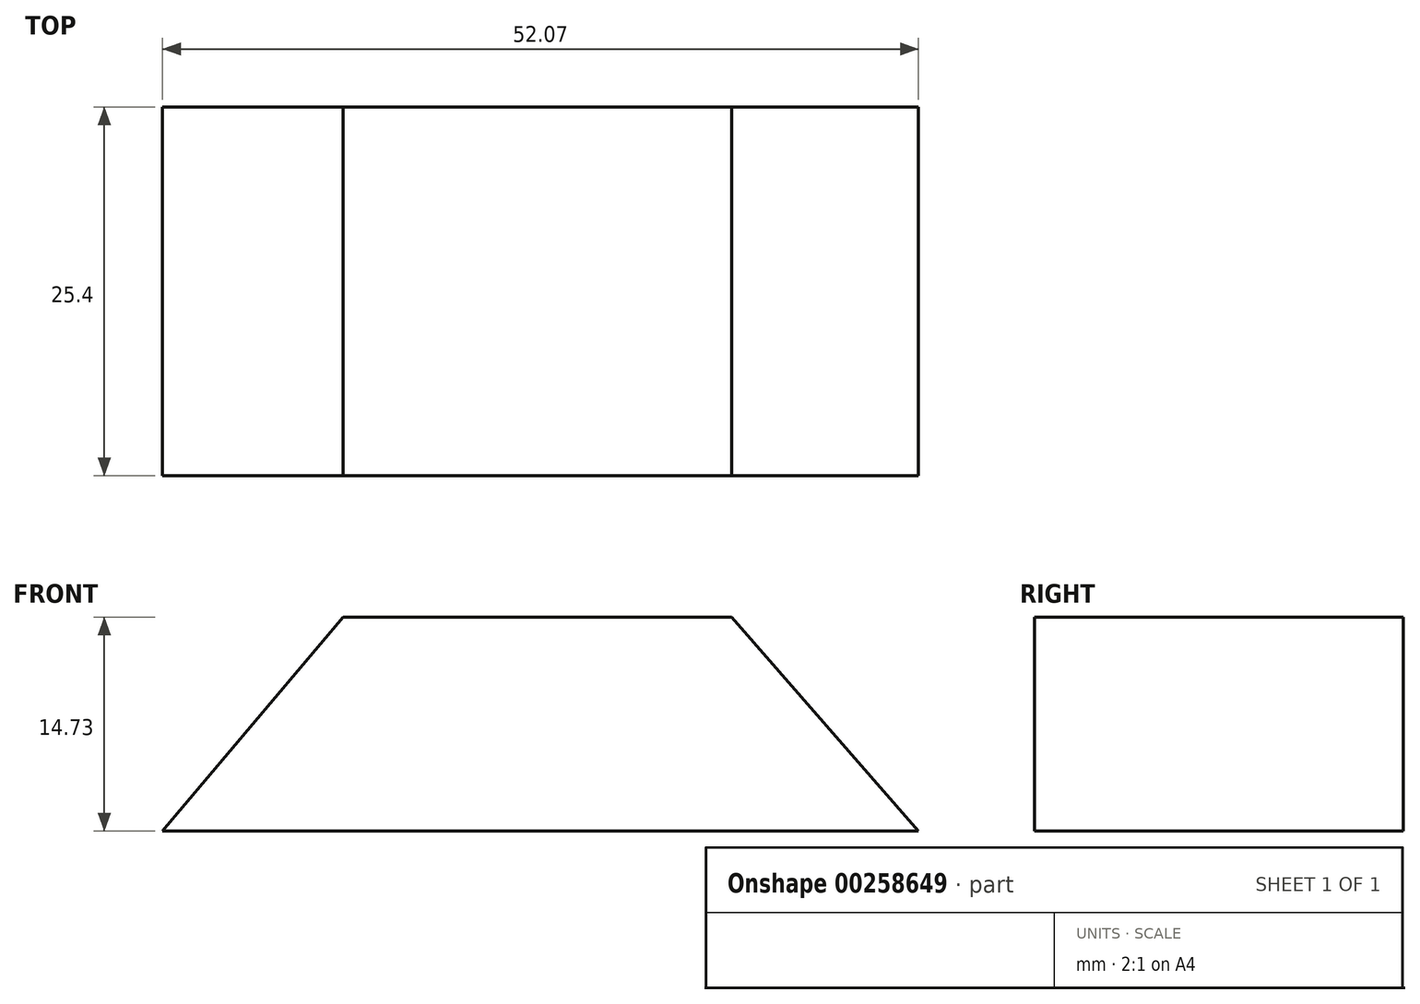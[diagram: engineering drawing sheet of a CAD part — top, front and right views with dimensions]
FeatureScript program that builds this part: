
annotation { "Feature Type Name" : "Feature", "Feature Type Description" : "" }
export const myFeature = defineFeature(function(context is Context, id is Id, definition is map)
    precondition{}
    {
        {
            var Q0;
            Q0=qCreatedBy(makeId("Front.planeOp"),FACE);
            var sketch = newSketch(context, id + "F0", { "sketchPlane" : qUnion([Q0])});
            skLineSegment(sketch, "E0", {"start": v(25.93, 27.8) * mm, "end": v(-26.14, 27.8) * mm});
            skLineSegment(sketch, "E1", {"start": v(-26.14, 27.8) * mm, "end": v(-13.7, 42.53) * mm});
            skLineSegment(sketch, "E2", {"start": v(-13.7, 42.53) * mm, "end": v(13.07, 42.53) * mm});
            skLineSegment(sketch, "E3", {"start": v(13.07, 42.53) * mm, "end": v(25.93, 27.8) * mm});
            skSolve(sketch);
        }
        {
            var Q0;
            Q0=makeQuery(id+"F0.imprint","IMPRINT",FACE,{"disambiguationData":[TD([[makeQuery(id+"F0.imprint","IMPRINT",EDGE,{"derivedFrom":sQuery(id+"F0.wireOp",EDGE,"E0")}),-1.0]])]});
            extrude(context, id + "F1", {"entities" : qUnion([Q0]), "depth" : 10.16 * mm});
        }
        {
            var Q0;
            Q0=makeQuery(id+"F1.opExtrude","CAP_FACE",FACE,{"disambiguationData":[OSD([sQuery(id+"F0.wireOp",EDGE,"E0"),sQuery(id+"F0.wireOp",EDGE,"E1"),sQuery(id+"F0.wireOp",EDGE,"E2"),sQuery(id+"F0.wireOp",EDGE,"E3")])],"isStart":false});
            extrude(context, id + "F2", {"entities" : qUnion([Q0]), "operationType" : NewBodyOperationType.ADD, "depth" : 15.24 * mm});
        }
    });
